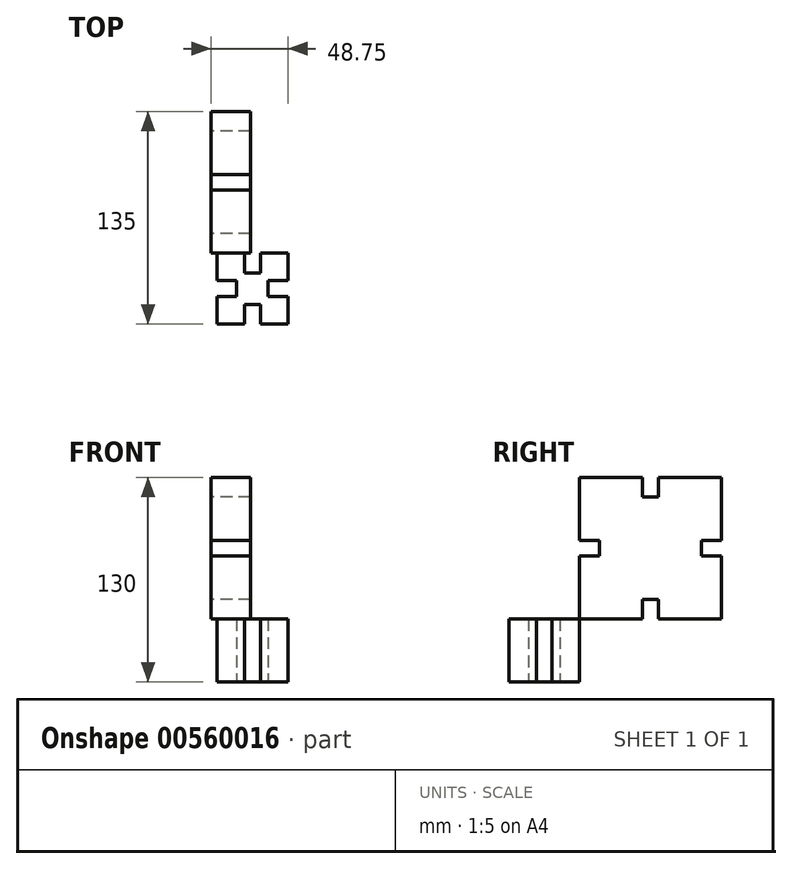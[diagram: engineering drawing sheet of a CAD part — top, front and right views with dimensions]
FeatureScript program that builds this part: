
annotation { "Feature Type Name" : "Feature", "Feature Type Description" : "" }
export const myFeature = defineFeature(function(context is Context, id is Id, definition is map)
    precondition{}
    {
        {
            var Q0;
            Q0=qCreatedBy(makeId("Top.planeOp"),FACE);
            var sketch = newSketch(context, id + "F0", { "sketchPlane" : qUnion([Q0])});
            skLineSegment(sketch, "E0", {"start": v(0, 45) * mm, "end": v(17.5, 45) * mm});
            skLineSegment(sketch, "E1", {"start": v(17.5, 45) * mm, "end": v(17.5, 32.5) * mm});
            skLineSegment(sketch, "E2", {"start": v(17.5, 32.5) * mm, "end": v(27.5, 32.5) * mm});
            skLineSegment(sketch, "E3", {"start": v(27.5, 32.5) * mm, "end": v(27.5, 45) * mm});
            skLineSegment(sketch, "E4", {"start": v(27.5, 45) * mm, "end": v(45, 45) * mm});
            skLineSegment(sketch, "E5", {"start": v(45, 45) * mm, "end": v(45, 27.5) * mm});
            skLineSegment(sketch, "E6", {"start": v(45, 27.5) * mm, "end": v(32.5, 27.5) * mm});
            skLineSegment(sketch, "E7", {"start": v(32.5, 27.5) * mm, "end": v(32.5, 17.5) * mm});
            skLineSegment(sketch, "E8", {"start": v(32.5, 17.5) * mm, "end": v(45, 17.5) * mm});
            skLineSegment(sketch, "E9", {"start": v(45, 17.5) * mm, "end": v(45, 0) * mm});
            skLineSegment(sketch, "E10", {"start": v(45, 0) * mm, "end": v(27.5, 0) * mm});
            skLineSegment(sketch, "E11", {"start": v(27.5, 0) * mm, "end": v(27.5, 12.5) * mm});
            skLineSegment(sketch, "E12", {"start": v(27.5, 12.5) * mm, "end": v(17.5, 12.5) * mm});
            skLineSegment(sketch, "E13", {"start": v(17.5, 12.5) * mm, "end": v(17.5, 0) * mm});
            skLineSegment(sketch, "E14", {"start": v(17.5, 0) * mm, "end": v(0, 0) * mm});
            skLineSegment(sketch, "E15", {"start": v(0, 0) * mm, "end": v(0, 17.5) * mm});
            skLineSegment(sketch, "E16", {"start": v(0, 17.5) * mm, "end": v(12.5, 17.5) * mm});
            skLineSegment(sketch, "E17", {"start": v(12.5, 17.5) * mm, "end": v(12.5, 27.5) * mm});
            skLineSegment(sketch, "E18", {"start": v(12.5, 27.5) * mm, "end": v(0, 27.5) * mm});
            skLineSegment(sketch, "E19", {"start": v(0, 27.5) * mm, "end": v(0, 45) * mm});
            skLineSegment(sketch, "E20", {"start": v(0, 0) * mm, "end": v(0, 45) * mm, "construction": true});
            skLineSegment(sketch, "E21", {"start": v(0, 0) * mm, "end": v(45, 0) * mm, "construction": true});
            skPoint(sketch, "E22.0", {"position": v(0, 0) * mm});
            skLineSegment(sketch, "E23", {"start": v(12.5, 27.5) * mm, "end": v(17.5, 32.5) * mm, "construction": true});
            skLineSegment(sketch, "E24", {"start": v(27.5, 32.5) * mm, "end": v(32.5, 27.5) * mm, "construction": true});
            skLineSegment(sketch, "E25", {"start": v(12.5, 17.5) * mm, "end": v(17.5, 12.5) * mm, "construction": true});
            skSolve(sketch);
        }
        {
            var Q0;
            Q0 = qSketchRegion(id + "F0", true);
            extrude(context, id + "F1", {"entities" : qUnion([Q0]), "depth" : 40 * mm, "offsetDistance" : 25 * mm});
        }
        {
            var Q0;
            Q0=qCreatedBy(makeId("Right.planeOp"),FACE);
            var sketch = newSketch(context, id + "F2", { "sketchPlane" : qUnion([Q0])});
            skLineSegment(sketch, "E26", {"start": v(-148.47, 62.07) * mm, "end": v(-108.47, 62.07) * mm});
            skLineSegment(sketch, "E27", {"start": v(-108.47, 62.07) * mm, "end": v(-108.47, 49.57) * mm});
            skLineSegment(sketch, "E28", {"start": v(-108.47, 49.57) * mm, "end": v(-98.47, 49.57) * mm});
            skLineSegment(sketch, "E29", {"start": v(-98.47, 49.57) * mm, "end": v(-98.47, 62.07) * mm});
            skLineSegment(sketch, "E30", {"start": v(-98.47, 62.07) * mm, "end": v(-58.47, 62.07) * mm});
            skLineSegment(sketch, "E31", {"start": v(-58.47, 62.07) * mm, "end": v(-58.47, 22.07) * mm});
            skLineSegment(sketch, "E32", {"start": v(-58.47, 22.07) * mm, "end": v(-70.97, 22.07) * mm});
            skLineSegment(sketch, "E33", {"start": v(-70.97, 22.07) * mm, "end": v(-70.97, 12.07) * mm});
            skLineSegment(sketch, "E34", {"start": v(-70.97, 12.07) * mm, "end": v(-58.47, 12.07) * mm});
            skLineSegment(sketch, "E35", {"start": v(-58.47, 12.07) * mm, "end": v(-58.47, -27.93) * mm});
            skLineSegment(sketch, "E36", {"start": v(-58.47, -27.93) * mm, "end": v(-98.47, -27.93) * mm});
            skLineSegment(sketch, "E37", {"start": v(-98.47, -27.93) * mm, "end": v(-98.47, -15.43) * mm});
            skLineSegment(sketch, "E38", {"start": v(-98.47, -15.43) * mm, "end": v(-108.47, -15.43) * mm});
            skLineSegment(sketch, "E39", {"start": v(-108.47, -15.43) * mm, "end": v(-108.47, -27.93) * mm});
            skLineSegment(sketch, "E40", {"start": v(-108.47, -27.93) * mm, "end": v(-148.47, -27.93) * mm});
            skLineSegment(sketch, "E41", {"start": v(-148.47, -27.93) * mm, "end": v(-148.47, 12.07) * mm});
            skLineSegment(sketch, "E42", {"start": v(-148.47, 12.07) * mm, "end": v(-135.97, 12.07) * mm});
            skLineSegment(sketch, "E43", {"start": v(-135.97, 12.07) * mm, "end": v(-135.97, 22.07) * mm});
            skLineSegment(sketch, "E44", {"start": v(-135.97, 22.07) * mm, "end": v(-148.47, 22.07) * mm});
            skLineSegment(sketch, "E45", {"start": v(-148.47, 22.07) * mm, "end": v(-148.47, 62.07) * mm});
            skLineSegment(sketch, "E46", {"start": v(-148.47, -27.93) * mm, "end": v(-148.47, 62.07) * mm, "construction": true});
            skLineSegment(sketch, "E47", {"start": v(-148.47, -27.93) * mm, "end": v(-58.47, -27.93) * mm, "construction": true});
            skPoint(sketch, "E48.0", {"position": v(-148.47, -5.43) * mm});
            skLineSegment(sketch, "E49", {"start": v(-135.97, 22.07) * mm, "end": v(-108.47, 49.57) * mm, "construction": true});
            skLineSegment(sketch, "E50", {"start": v(-98.47, 49.57) * mm, "end": v(-70.97, 22.07) * mm, "construction": true});
            skLineSegment(sketch, "E51", {"start": v(-135.97, 12.07) * mm, "end": v(-108.47, -15.43) * mm, "construction": true});
            skSolve(sketch);
        }
        {
            var Q0;
            Q0 = qSketchRegion(id + "F2", true);
            extrude(context, id + "F3", {"entities" : qUnion([Q0]), "depth" : 25 * mm, "offsetDistance" : 25 * mm});
        }
        {
            var Q0;
            Q0=makeQuery(id+"F3.opExtrude","SWEPT_EDGE",EDGE,{"disambiguationData":[OSD([sQuery(id+"F2.wireOp",EDGE,"E40"),sQuery(id+"F2.wireOp",EDGE,"E41")])]});
            cPoint(context, id + "F4", {"entities" : qUnion([Q0]), "parameter" : 0.5});
        }
        {
            var Q0;
            Q0=makeQuery(id+"F1.opExtrude","CAP_EDGE",EDGE,{"disambiguationData":[OSD([sQuery(id+"F0.wireOp",EDGE,"E0")])],"isStart":false});
            cPoint(context, id + "F5", {"entities" : qUnion([Q0]), "parameter" : 0.5});
        }
        {
            var Q0;
            Q0=makeQuery(id+"F3.opExtrude","SWEPT_BODY",BODY,{"disambiguationData":[OSD([sQuery(id+"F2.wireOp",EDGE,"E26"),sQuery(id+"F2.wireOp",EDGE,"E27"),sQuery(id+"F2.wireOp",EDGE,"E28"),sQuery(id+"F2.wireOp",EDGE,"E29"),sQuery(id+"F2.wireOp",EDGE,"E30"),sQuery(id+"F2.wireOp",EDGE,"E31"),sQuery(id+"F2.wireOp",EDGE,"E32"),sQuery(id+"F2.wireOp",EDGE,"E33"),sQuery(id+"F2.wireOp",EDGE,"E34"),sQuery(id+"F2.wireOp",EDGE,"E35"),sQuery(id+"F2.wireOp",EDGE,"E36"),sQuery(id+"F2.wireOp",EDGE,"E37"),sQuery(id+"F2.wireOp",EDGE,"E38"),sQuery(id+"F2.wireOp",EDGE,"E39"),sQuery(id+"F2.wireOp",EDGE,"E40"),sQuery(id+"F2.wireOp",EDGE,"E41"),sQuery(id+"F2.wireOp",EDGE,"E42"),sQuery(id+"F2.wireOp",EDGE,"E43"),sQuery(id+"F2.wireOp",EDGE,"E44"),sQuery(id+"F2.wireOp",EDGE,"E45")])]});
            var Q1;
            Q1 = qCreatedBy(id + "F4" ,VERTEX);
            var Q2;
            Q2 = qCreatedBy(id + "F5" ,VERTEX);
            transform(context, id + "F6", {"entities" : qUnion([Q0]), "transformType" : TransformType.TRANSLATION_ENTITY, "oppositeDirectionEntity" : false, "transformLine" : qUnion([Q1, Q2]), "makeCopy" : false});
        }
    });
